# Revit family: FU_Chair_Sandler_Celina 2-12
name_source: partatom
category: Furniture
units: mm (PartAtom-declared; Revit-internal decimal feet)

## family parameters
Always vertical = Yes
Cut with Voids When Loaded = No
OmniClass Number = 23.40.20.00
OmniClass Title = General Furniture and Specialties
Room Calculation Point = No
Shared = No
Work Plane-Based = No

## types (1)
- Celina 2.12
    Arm Width = 650 mm  [stored 2.13255 ft]
    Default Elevation = 0 mm  [stored 0 ft]
    Depth = 550 mm  [stored 1.80446 ft]
    Description = Armchair with seat and wooden back. The frame is in solid beech.
    Frame = Wood - Beech - Black Stain
    Height = 820 mm  [stored 2.69029 ft]
    Manufacturer = Sandler
    Model = Celina 2.12
    URL = https://www.sandlerseating.com
    Width = 500 mm  [stored 1.64042 ft]

note: [stored X ft] marks values corroborated as IEEE doubles in the binary element streams (Revit-internal decimal feet)

## geometry (parser evidence)
native form markers: Sweep x9
no freeform markers — native parametric forms only
